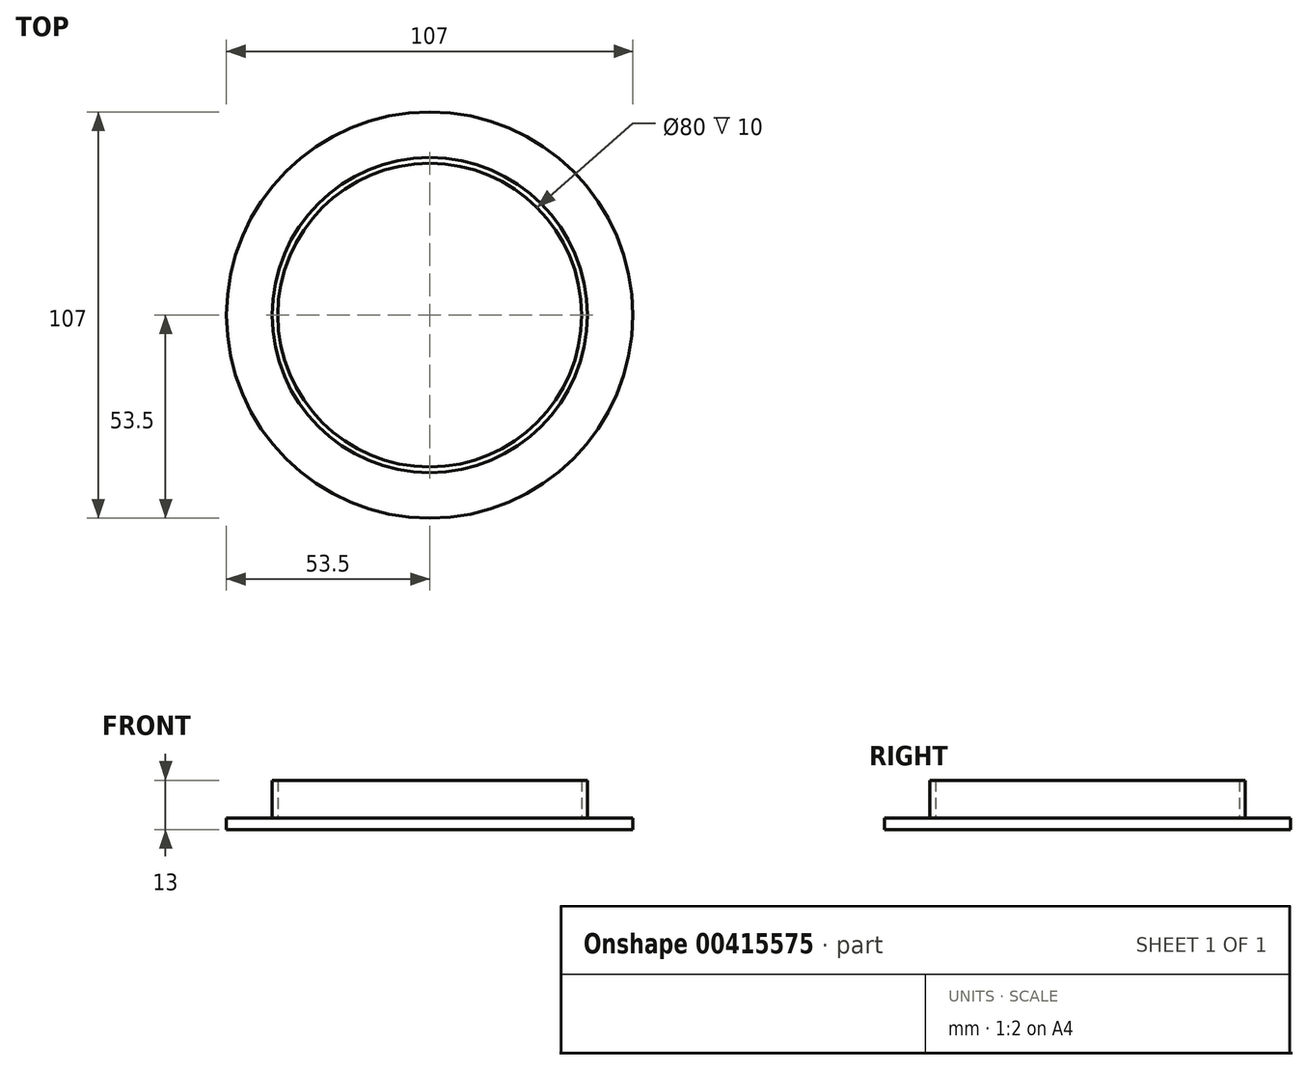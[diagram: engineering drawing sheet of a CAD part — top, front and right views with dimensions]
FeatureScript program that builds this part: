
annotation { "Feature Type Name" : "Feature", "Feature Type Description" : "" }
export const myFeature = defineFeature(function(context is Context, id is Id, definition is map)
    precondition{}
    {
        {
            var Q0;
            Q0=qCreatedBy(makeId("Top.planeOp"),FACE);
            var sketch = newSketch(context, id + "F0", { "sketchPlane" : qUnion([Q0])});
            skCircle(sketch, "E0", {"center": v(0, 0) * mm, "radius": 53.5 * mm});
            skCircle(sketch, "E1", {"center": v(0, 0) * mm, "radius": 41.4 * mm});
            skCircle(sketch, "E2", {"center": v(0, 0) * mm, "radius": 39.9 * mm});
            skSolve(sketch);
        }
        {
            var Q0;
            Q0=makeQuery(id+"F0.imprint","IMPRINT",FACE,{"disambiguationData":[TD([[makeQuery(id+"F0.imprint","IMPRINT",EDGE,{"derivedFrom":sQuery(id+"F0.wireOp",EDGE,"E0")}),1.0]])]});
            var Q1;
            Q1=makeQuery(id+"F0.imprint","IMPRINT",FACE,{"disambiguationData":[TD([[makeQuery(id+"F0.imprint","IMPRINT",EDGE,{"derivedFrom":sQuery(id+"F0.wireOp",EDGE,"E1")}),1.0]])]});
            var Q2;
            Q2=makeQuery(id+"F0.imprint","IMPRINT",FACE,{"disambiguationData":[TD([[makeQuery(id+"F0.imprint","IMPRINT",EDGE,{"derivedFrom":sQuery(id+"F0.wireOp",EDGE,"E2")}),1.0]])]});
            extrude(context, id + "F1", {"entities" : qUnion([Q0, Q1, Q2]), "depth" : 3 * mm});
        }
        {
            var Q0;
            Q0=makeQuery(id+"F1.opExtrude","CAP_FACE",FACE,{"disambiguationData":[OSD([sQuery(id+"F0.wireOp",EDGE,"E0")])],"isStart":false});
            var sketch = newSketch(context, id + "F2", { "sketchPlane" : qUnion([Q0])});
            skCircle(sketch, "E3", {"center": v(0, 0) * mm, "radius": 41.5 * mm});
            skCircle(sketch, "E4", {"center": v(0, 0) * mm, "radius": 40 * mm});
            skSolve(sketch);
        }
        {
            var Q0;
            Q0=makeQuery(id+"F2.imprint","IMPRINT",FACE,{"disambiguationData":[TD([[makeQuery(id+"F2.imprint","IMPRINT",EDGE,{"derivedFrom":sQuery(id+"F2.wireOp",EDGE,"E3")}),1.0]])]});
            extrude(context, id + "F3", {"entities" : qUnion([Q0]), "operationType" : NewBodyOperationType.ADD, "depth" : 10 * mm});
        }
    });
